# Revit family: Hager-Pablo-IP40-Plain_Door-vuoto-IT-it
name_source: partatom
category: Electrical Equipment
units: mm (PartAtom-declared; Revit-internal decimal feet)

## family parameters
Cut with Voids When Loaded = No
Host = Face
Panel Configuration = Two Columns, Circuits Across
Part Type = Panelboard
Room Calculation Point = No
Round Connector Dimension = Use Diameter
Shared = No

## types (18) — shared parameters
EF000003 - Tipo di montaggio = EV001247 - apparente/incassato
EF000007 - colore = EV000202 - bianco
EF000049 - profondità = 25 mm  [stored 0.082021 ft]
EF000116 - numero RAL = 9016
EF000118 - con piastra di montaggio = No
EF000218 - profondità di incasso = 16 mm  [stored 0.0524934 ft]
EF000339 - tipo di copertura = EV004216 - porta
EF001062 - esecuzione EMC = No
EF001088 - possibilità di applicazione = Yes
EF001131 - profondità interna = 16 mm  [stored 0.0524934 ft]
EF001134 - barra DIN = Yes
EF001596 - Attacco Lampada = EV000139 - plastica
EF004462 - tipo di chiusura = EV001412 - cilindro
EF005474 - grado di protezione (IP) = EV006415 - IP40
EF006244 - coperchio/porta trasparente = No
EF006306 - con serratura = No
EF009212 - esecuzione coperchio = EV000116 - chiuso
EF015776 - Morsettiera di terra = No
EF015777 - Morsettiera neutra = No
EF015941 - Segnale di passaggio porta = No
HG000002 - Con porta = Yes
HG000003 - Gamma = Pablo
HG000005 - Spessore = 3 mm  [stored 0.00984252 ft]
HG000009 - Porta doppia a battente = No
HG000010 - Porte asimmetriche = No
HG000011 - File vuote nella parte basse = No
HG000017 - Distanza tra i poli = 18 mm  [stored 0.0590551 ft]
Manufacturer = Hager
Type Comments = Pablo
zero-valued in all types: Default Elevation, HG000001 - Numero di colonne, HG000007 - Numero di colonne vuote, HG000008 - Numero di file vuote

## per-type parameters (varying)
| type | EF000008 - Larghezza | EF000040 - Altezza | EF000266 - numero di file | EF000332 - Altezza della parte incassata | EF000846 - larghezza di montaggio | EF002950 - Numero moduli DIN | HG000004 - Codice produttore | HG000006 - Ad incasso | Model |
| A parete IP40 L175 A191 P25 4 Unità di divisione - B04941 | 175 mm  [stored 0.574147 ft] | 191 mm  [stored 0.62664 ft] | 1 | 160 mm  [stored 0.524934 ft] | 175 mm  [stored 0.574147 ft] | 4 | B04941 | No | B04941 |
| A parete IP40 L211 A191 P25 6 Unità di divisione - B04942 | 211 mm  [stored 0.692257 ft] | 191 mm  [stored 0.62664 ft] | 1 | 160 mm  [stored 0.524934 ft] | 211 mm  [stored 0.692257 ft] | 6 | B04942 | No | B04942 |
| A parete IP40 L280 A235 P25 8 Unità di divisione - B04943 | 280 mm  [stored 0.918635 ft] | 235 mm  [stored 0.770997 ft] | 1 | 160 mm  [stored 0.524934 ft] | 280 mm  [stored 0.918635 ft] | 8 | B04943 | No | B04943 |
| A parete IP40 L352 A275 P25 12 Unità di divisione - B04944 | 352 mm  [stored 1.15486 ft] | 275 mm | 1 | 160 mm  [stored 0.524934 ft] | 352 mm  [stored 1.15486 ft] | 12 | B04944 | No | B04944 |
| A parete IP40 L352 A425 P25 12 Unità di divisione - B04946 | 352 mm  [stored 1.15486 ft] | 425 mm  [stored 1.39436 ft] | 2 | 405 mm | 352 mm  [stored 1.15486 ft] | 12 | B04946 | No | B04946 |
| A parete IP40 L352 A575 P25 12 Unità di divisione - B04947 | 352 mm  [stored 1.15486 ft] | 575 mm  [stored 1.88648 ft] | 3 | 405 mm | 352 mm  [stored 1.15486 ft] | 12 | B04947 | No | B04947 |
| A parete IP40 L460 A275 P25 18 Unità di divisione - B04945 | 460 mm  [stored 1.50919 ft] | 275 mm | 1 | 160 mm  [stored 0.524934 ft] | 460 mm  [stored 1.50919 ft] | 18 | B04945 | No | B04945 |
| A parete IP40 L460 A575 P25 18 Unità di divisione - B04948 | 460 mm  [stored 1.50919 ft] | 575 mm  [stored 1.88648 ft] | 3 | 405 mm | 460 mm  [stored 1.50919 ft] | 18 | B04948 | No | B04948 |
| A parete IP40 L460 A725 P25 18 Unità di divisione - B04949 | 460 mm  [stored 1.50919 ft] | 725 mm  [stored 2.37861 ft] | 4 | 630 mm  [stored 2.06693 ft] | 460 mm  [stored 1.50919 ft] | 18 | B04949 | No | B04949 |
| Incassato IP40 L175 A191 P25 4 Unità di divisione - B04941 | 175 mm  [stored 0.574147 ft] | 191 mm  [stored 0.62664 ft] | 1 | 160 mm  [stored 0.524934 ft] | 175 mm  [stored 0.574147 ft] | 4 | B04941 | Yes | B04941 |
| Incassato IP40 L211 A191 P25 6 Unità di divisione - B04942 | 211 mm  [stored 0.692257 ft] | 191 mm  [stored 0.62664 ft] | 1 | 160 mm  [stored 0.524934 ft] | 211 mm  [stored 0.692257 ft] | 6 | B04942 | Yes | B04942 |
| Incassato IP40 L280 A235 P25 8 Unità di divisione - B04943 | 280 mm  [stored 0.918635 ft] | 235 mm  [stored 0.770997 ft] | 1 | 160 mm  [stored 0.524934 ft] | 280 mm  [stored 0.918635 ft] | 8 | B04943 | Yes | B04943 |
| Incassato IP40 L352 A275 P25 12 Unità di divisione - B04944 | 352 mm  [stored 1.15486 ft] | 275 mm | 1 | 160 mm  [stored 0.524934 ft] | 352 mm  [stored 1.15486 ft] | 12 | B04944 | Yes | B04944 |
| Incassato IP40 L352 A425 P25 12 Unità di divisione - B04946 | 352 mm  [stored 1.15486 ft] | 425 mm  [stored 1.39436 ft] | 2 | 405 mm | 352 mm  [stored 1.15486 ft] | 12 | B04946 | Yes | B04946 |
| Incassato IP40 L352 A575 P25 12 Unità di divisione - B04947 | 352 mm  [stored 1.15486 ft] | 575 mm  [stored 1.88648 ft] | 3 | 405 mm | 352 mm  [stored 1.15486 ft] | 12 | B04947 | Yes | B04947 |
| Incassato IP40 L460 A275 P25 18 Unità di divisione - B04945 | 460 mm  [stored 1.50919 ft] | 275 mm | 1 | 160 mm  [stored 0.524934 ft] | 460 mm  [stored 1.50919 ft] | 18 | B04945 | Yes | B04945 |
| Incassato IP40 L460 A575 P25 18 Unità di divisione - B04948 | 460 mm  [stored 1.50919 ft] | 575 mm  [stored 1.88648 ft] | 3 | 405 mm | 460 mm  [stored 1.50919 ft] | 18 | B04948 | Yes | B04948 |
| Incassato IP40 L460 A725 P25 18 Unità di divisione - B04949 | 460 mm  [stored 1.50919 ft] | 725 mm  [stored 2.37861 ft] | 4 | 630 mm  [stored 2.06693 ft] | 460 mm  [stored 1.50919 ft] | 18 | B04949 | Yes | B04949 |

note: [stored X ft] marks values corroborated as IEEE doubles in the binary element streams (Revit-internal decimal feet)

## geometry (parser evidence)
native form markers: Sweep x17
no freeform markers — native parametric forms only
